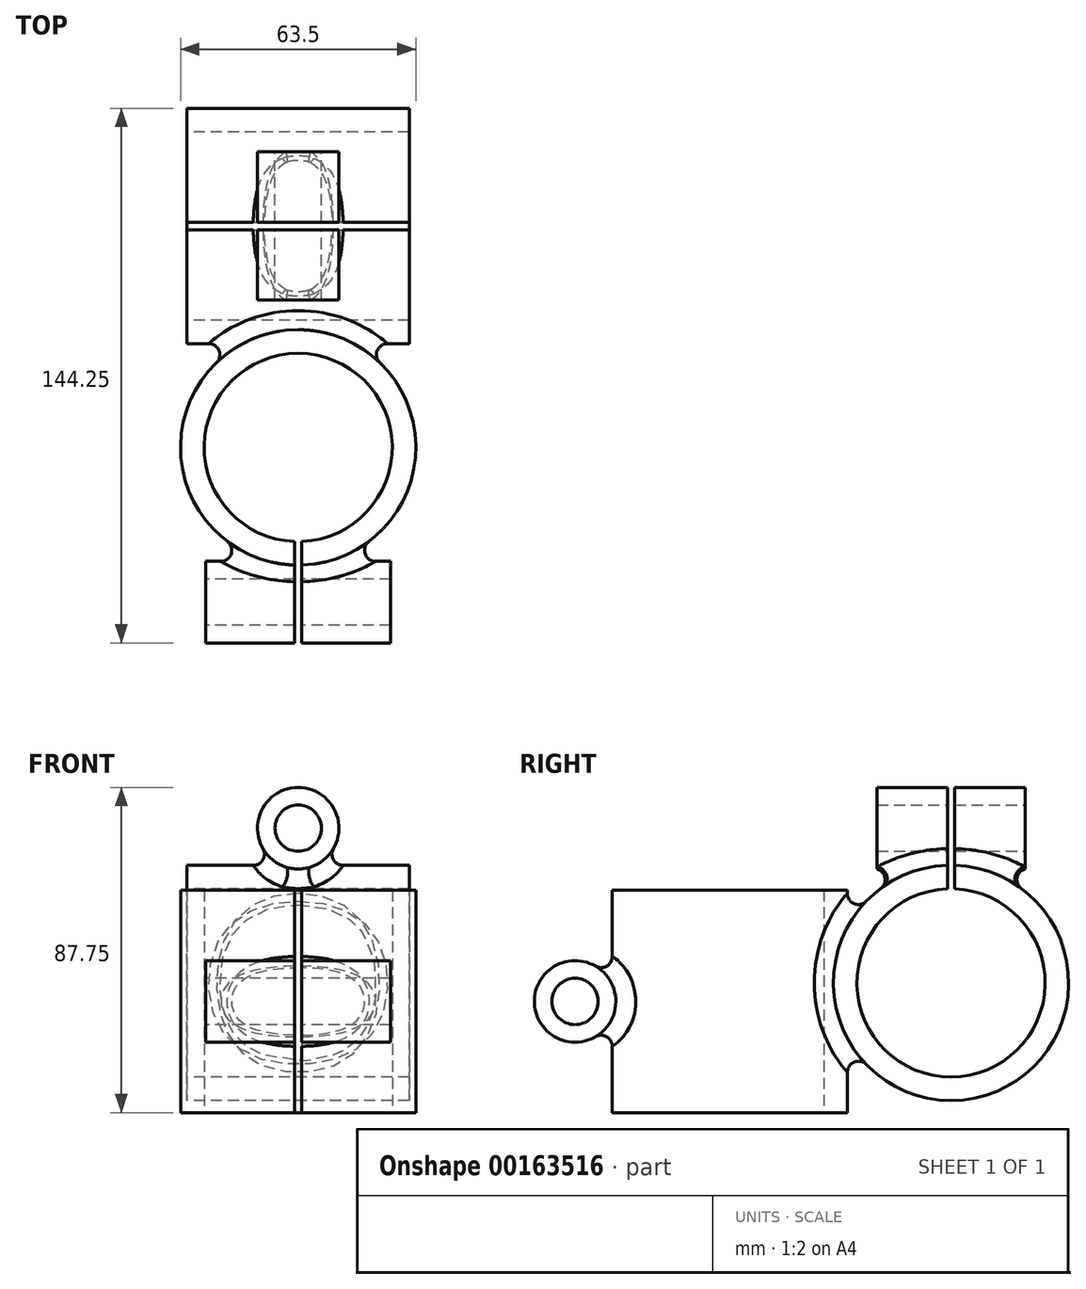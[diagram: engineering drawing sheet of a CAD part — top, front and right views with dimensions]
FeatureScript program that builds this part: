
annotation { "Feature Type Name" : "Feature", "Feature Type Description" : "" }
export const myFeature = defineFeature(function(context is Context, id is Id, definition is map)
    precondition{}
    {
        {
            var Q0;
            Q0=qCreatedBy(makeId("Top.planeOp"),FACE);
            var sketch = newSketch(context, id + "F0", { "sketchPlane" : qUnion([Q0])});
            skCircle(sketch, "E0", {"center": v(0, 0) * mm, "radius": 31.75 * mm});
            skCircle(sketch, "E1", {"center": v(0, 0) * mm, "radius": 25.4 * mm});
            skSolve(sketch);
        }
        {
            var Q0;
            Q0 = qSketchRegion(id + "F0", true);
            extrude(context, id + "F1", {"entities" : qUnion([Q0]), "depth" : 60 * mm});
        }
        {
            var Q0;
            Q0=qCreatedBy(makeId("Right.planeOp"),FACE);
            var sketch = newSketch(context, id + "F2", { "sketchPlane" : qUnion([Q0])});
            skLineSegment(sketch, "E2", {"start": v(-31.75, 0) * mm, "end": v(-31.75, 60) * mm, "construction": true});
            skLineSegment(sketch, "E3", {"start": v(-65.95, 30) * mm, "end": v(45.45, 30) * mm, "construction": true});
            skLineSegment(sketch, "E4", {"start": v(-41.75, 59.34) * mm, "end": v(-41.75, 0) * mm, "construction": true});
            skCircle(sketch, "E5", {"center": v(-41.75, 30) * mm, "radius": 11 * mm});
            skCircle(sketch, "E6", {"center": v(-41.75, 30) * mm, "radius": 6.25 * mm});
            skSolve(sketch);
        }
        {
            var Q0;
            Q0 = qSketchRegion(id + "F2", true);
            extrude(context, id + "F3", {"entities" : qUnion([Q0]), "operationType" : NewBodyOperationType.ADD, "endBound" : BoundingType.SYMMETRIC, "depth" : 50 * mm});
        }
        {
            var Q0;
            Q0=makeQuery(id+"F3.boolean.opBoolean","INTERSECT",EDGE,{"derivedFrom":[makeQuery(id+"F1.opExtrude","SWEPT_FACE",FACE,{"disambiguationData":[OSD([sQuery(id+"F0.wireOp",EDGE,"E0")])]}),makeQuery(id+"F3.opExtrude","SWEPT_FACE",FACE,{"disambiguationData":[OSD([sQuery(id+"F2.wireOp",EDGE,"E5")])]})]});
            fillet(context, id + "F4", {"entities" : qUnion([Q0]), "radius" : 3 * mm, "tangentPropagation" : true, "allowEdgeOverflow" : false});
        }
        {
            var Q0;
            Q0=qCreatedBy(makeId("Right.planeOp"),FACE);
            var sketch = newSketch(context, id + "F5", { "sketchPlane" : qUnion([Q0])});
            skLineSegment(sketch, "E7", {"start": v(31.75, 60) * mm, "end": v(31.75, 0) * mm, "construction": true});
            skCircle(sketch, "E8", {"center": v(59.75, 35) * mm, "radius": 31.75 * mm});
            skCircle(sketch, "E9", {"center": v(59.75, 35) * mm, "radius": 25.4 * mm});
            skSolve(sketch);
        }
        {
            var Q0;
            Q0 = qSketchRegion(id + "F5", true);
            extrude(context, id + "F6", {"entities" : qUnion([Q0]), "operationType" : NewBodyOperationType.ADD, "endBound" : BoundingType.SYMMETRIC, "depth" : 60 * mm});
        }
        {
            var Q0;
            Q0=makeQuery(id+"F6.boolean.opBoolean","INTERSECT",EDGE,{"derivedFrom":[makeQuery(id+"F1.opExtrude","SWEPT_FACE",FACE,{"disambiguationData":[OSD([sQuery(id+"F0.wireOp",EDGE,"E0")])]}),makeQuery(id+"F6.opExtrude","SWEPT_FACE",FACE,{"disambiguationData":[OSD([sQuery(id+"F5.wireOp",EDGE,"E8")])]})]});
            fillet(context, id + "F7", {"entities" : qUnion([Q0]), "radius" : 3 * mm, "tangentPropagation" : true, "allowEdgeOverflow" : false});
        }
        {
            var Q0;
            Q0=qCreatedBy(makeId("Top.planeOp"),FACE);
            var sketch = newSketch(context, id + "F8", { "sketchPlane" : qUnion([Q0])});
            skLineSegment(sketch, "E10", {"start": v(0, -0.21) * mm, "end": v(0, -62.93) * mm, "construction": true});
            skLineSegment(sketch, "E11", {"start": v(-1, -0.66) * mm, "end": v(-1, -58.74) * mm});
            skLineSegment(sketch, "E12", {"start": v(1, -0.68) * mm, "end": v(1, -58.74) * mm});
            skLineSegment(sketch, "E13", {"start": v(-1, -0.66) * mm, "end": v(1, -0.68) * mm});
            skLineSegment(sketch, "E14", {"start": v(-1, -58.74) * mm, "end": v(1, -58.74) * mm});
            skPoint(sketch, "E15.orphan", {"position": v(1, -0.86) * mm});
            skPoint(sketch, "E16.orphan", {"position": v(19.86, -0.86) * mm});
            skSolve(sketch);
        }
        {
            var Q0;
            Q0 = qSketchRegion(id + "F8", true);
            extrude(context, id + "F9", {"entities" : qUnion([Q0]), "operationType" : NewBodyOperationType.REMOVE, "depth" : 60 * mm});
        }
        {
            var Q0;
            Q0=qCreatedBy(makeId("Front.planeOp"),FACE);
            var Q1;
            Q1=sQuery(id+"F5.wireOp",VERTEX,"E8.center");
            cPlane(context, id + "F10", {"entities" : qUnion([Q0, Q1]), "cplaneType" : CPlaneType.PLANE_POINT, "offset" : 25 * mm, "width" : 150 * mm, "height" : 150 * mm});
        }
        {
            var Q0;
            Q0=qCreatedBy(id+"F10.planeOp",FACE);
            var sketch = newSketch(context, id + "F11", { "sketchPlane" : qUnion([Q0])});
            skLineSegment(sketch, "E17", {"start": v(-30, 66.75) * mm, "end": v(30, 66.75) * mm, "construction": true});
            skLineSegment(sketch, "E18", {"start": v(0, 66.75) * mm, "end": v(0, 94.67) * mm, "construction": true});
            skCircle(sketch, "E19", {"center": v(0, 76.75) * mm, "radius": 11 * mm});
            skCircle(sketch, "E20", {"center": v(0, 76.75) * mm, "radius": 6.25 * mm});
            skSolve(sketch);
        }
        {
            var Q0;
            Q0 = qSketchRegion(id + "F11", true);
            extrude(context, id + "F12", {"entities" : qUnion([Q0]), "operationType" : NewBodyOperationType.ADD, "endBound" : BoundingType.SYMMETRIC, "depth" : 40 * mm});
        }
        {
            var Q0;
            {var subQ1=sQuery(id+"F5.wireOp",EDGE,"E8");Q0=makeQuery(id+"F12.boolean.opBoolean","INTERSECT",EDGE,{"derivedFrom":[makeQuery(id+"F6.boolean.opBoolean","SPLIT",FACE,{"disambiguationData":[TD([makeQuery(id+"F1.opExtrude","SWEPT_FACE",FACE,{"disambiguationData":[OSD([sQuery(id+"F0.wireOp",EDGE,"E0")])]})])],"derivedFrom":makeQuery(id+"F6.opExtrude","SWEPT_FACE",FACE,{"disambiguationData":[OSD([subQ1])]})}),makeQuery(id+"F12.opExtrude","SWEPT_FACE",FACE,{"disambiguationData":[OSD([sQuery(id+"F11.wireOp",EDGE,"E19")])]})]});}
            fillet(context, id + "F13", {"entities" : qUnion([Q0]), "radius" : 3 * mm, "tangentPropagation" : true, "allowEdgeOverflow" : false});
        }
        {
            var Q0;
            Q0=qCreatedBy(makeId("Right.planeOp"),FACE);
            var sketch = newSketch(context, id + "F14", { "sketchPlane" : qUnion([Q0])});
            skLineSegment(sketch, "E21", {"start": v(59.75, 49.54) * mm, "end": v(59.75, 93.88) * mm, "construction": true});
            skLineSegment(sketch, "E22", {"start": v(60.75, 93.88) * mm, "end": v(60.75, 49.54) * mm});
            skLineSegment(sketch, "E23", {"start": v(58.75, 93.88) * mm, "end": v(58.75, 49.54) * mm});
            skLineSegment(sketch, "E24", {"start": v(58.75, 93.88) * mm, "end": v(60.75, 93.88) * mm});
            skLineSegment(sketch, "E25", {"start": v(58.75, 49.54) * mm, "end": v(60.75, 49.54) * mm});
            skSolve(sketch);
        }
        {
            var Q0;
            Q0 = qSketchRegion(id + "F14", true);
            extrude(context, id + "F15", {"entities" : qUnion([Q0]), "operationType" : NewBodyOperationType.REMOVE, "endBound" : BoundingType.SYMMETRIC, "depth" : 60 * mm});
        }
    });
